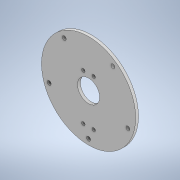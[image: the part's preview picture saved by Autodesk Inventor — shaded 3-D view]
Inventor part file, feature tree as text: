
AUTODESK INVENTOR PART (.ipt)
format: ipt  version: 2022 (Build 260153000, 153)  size: 137,728 bytes
history: native  units: mm
features: extrude x1
ambient origin geometry x8: Origin, YZ Plane, XZ Plane, XY Plane, X Axis, Y Axis, Z Axis, Center Point
bodies: Solid1 (feature_tree)
feature tree (1):
  extrude  "Extrusion1"  Depth=100.0mm
